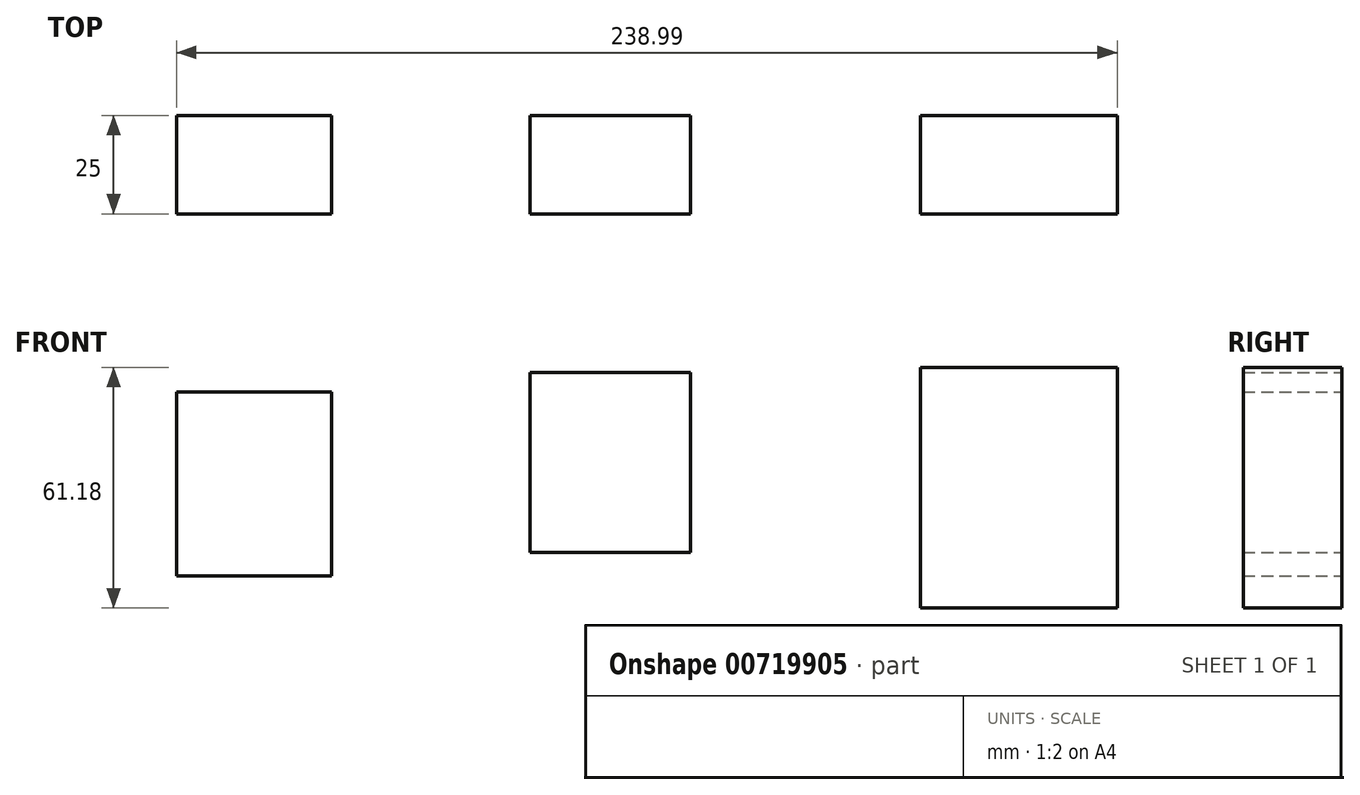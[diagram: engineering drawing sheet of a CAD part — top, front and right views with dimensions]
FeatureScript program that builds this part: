
annotation { "Feature Type Name" : "Feature", "Feature Type Description" : "" }
export const myFeature = defineFeature(function(context is Context, id is Id, definition is map)
    precondition{}
    {
        {
            var Q0;
            Q0=qCreatedBy(makeId("Front.planeOp"),FACE);
            var sketch = newSketch(context, id + "F0", { "sketchPlane" : qUnion([Q0])});
            skLineSegment(sketch, "E0.bottom", {"start": v(-130.68, 12.51) * mm, "end": v(-91.3, 12.51) * mm});
            skLineSegment(sketch, "E0.top", {"start": v(-130.68, 59.26) * mm, "end": v(-91.3, 59.26) * mm});
            skLineSegment(sketch, "E0.left", {"start": v(-130.68, 12.51) * mm, "end": v(-130.68, 59.26) * mm});
            skLineSegment(sketch, "E0.right", {"start": v(-91.3, 12.51) * mm, "end": v(-91.3, 59.26) * mm});
            skPoint(sketch, "E0.middle", {"position": v(-110.98, 35.89) * mm});
            skLineSegment(sketch, "E1.bottom", {"start": v(-40.89, 18.4) * mm, "end": v(-0.17, 18.4) * mm});
            skLineSegment(sketch, "E1.top", {"start": v(-40.89, 64.2) * mm, "end": v(-0.17, 64.2) * mm});
            skLineSegment(sketch, "E1.left", {"start": v(-40.89, 18.4) * mm, "end": v(-40.89, 64.2) * mm});
            skLineSegment(sketch, "E1.right", {"start": v(-0.17, 18.4) * mm, "end": v(-0.17, 64.2) * mm});
            skPoint(sketch, "E1.middle", {"position": v(-20.53, 41.3) * mm});
            skLineSegment(sketch, "E2.bottom", {"start": v(58.25, 4.3) * mm, "end": v(108.31, 4.3) * mm});
            skLineSegment(sketch, "E2.top", {"start": v(58.25, 65.48) * mm, "end": v(108.31, 65.48) * mm});
            skLineSegment(sketch, "E2.left", {"start": v(58.25, 4.3) * mm, "end": v(58.25, 65.48) * mm});
            skLineSegment(sketch, "E2.right", {"start": v(108.31, 4.3) * mm, "end": v(108.31, 65.48) * mm});
            skPoint(sketch, "E2.middle", {"position": v(83.28, 34.89) * mm});
            skSolve(sketch);
        }
        {
            var Q0;
            Q0=makeQuery(id+"F0.imprint","IMPRINT",FACE,{"disambiguationData":[TD([[makeQuery(id+"F0.imprint","IMPRINT",EDGE,{"derivedFrom":sQuery(id+"F0.wireOp",EDGE,"E0.bottom")}),1.0]])]});
            var Q1;
            Q1=makeQuery(id+"F0.imprint","IMPRINT",FACE,{"disambiguationData":[TD([[makeQuery(id+"F0.imprint","IMPRINT",EDGE,{"derivedFrom":sQuery(id+"F0.wireOp",EDGE,"E1.bottom")}),1.0]])]});
            var Q2;
            Q2=makeQuery(id+"F0.imprint","IMPRINT",FACE,{"disambiguationData":[TD([[makeQuery(id+"F0.imprint","IMPRINT",EDGE,{"derivedFrom":sQuery(id+"F0.wireOp",EDGE,"E2.bottom")}),1.0]])]});
            extrude(context, id + "F1", {"entities" : qUnion([Q0, Q1, Q2]), "depth" : 25 * mm, "offsetDistance" : 25 * mm});
        }
    });
